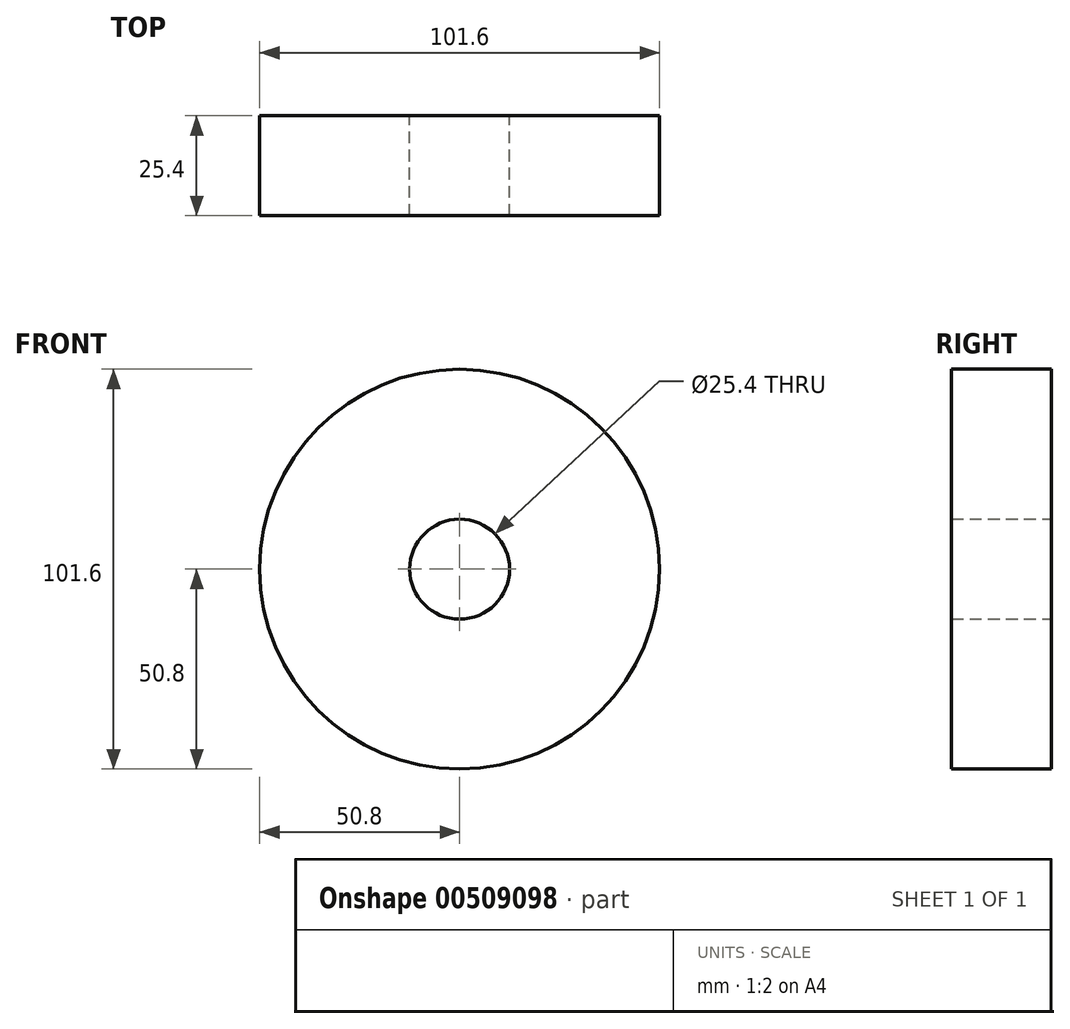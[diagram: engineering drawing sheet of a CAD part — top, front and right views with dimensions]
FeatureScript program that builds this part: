
annotation { "Feature Type Name" : "Feature", "Feature Type Description" : "" }
export const myFeature = defineFeature(function(context is Context, id is Id, definition is map)
    precondition{}
    {
        {
            var Q0;
            Q0=qCreatedBy(makeId("Front.planeOp"),FACE);
            var sketch = newSketch(context, id + "F0", { "sketchPlane" : qUnion([Q0])});
            skCircle(sketch, "E0", {"center": v(0, 0) * mm, "radius": 50.8 * mm});
            skCircle(sketch, "E1", {"center": v(0, 0) * mm, "radius": 12.7 * mm});
            skSolve(sketch);
        }
        {
            var Q0;
            Q0=makeQuery(id+"F0.imprint","IMPRINT",FACE,{"disambiguationData":[TD([[makeQuery(id+"F0.imprint","IMPRINT",EDGE,{"derivedFrom":sQuery(id+"F0.wireOp",EDGE,"E0")}),1.0]])]});
            extrude(context, id + "F1", {"entities" : qUnion([Q0]), "depth" : 25.4 * mm});
        }
    });
